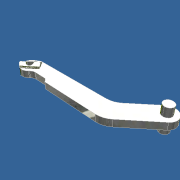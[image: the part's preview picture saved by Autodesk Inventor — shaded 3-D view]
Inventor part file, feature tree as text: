
AUTODESK INVENTOR PART (.ipt)
format: ipt  version: unknown  size: 225,280 bytes
history: native  units: mm
features: extrude x5, sketch x5, other x1
ambient origin geometry x8: Origin, YZ Plane, XZ Plane, XY Plane, X Axis, Y Axis, Z Axis, Center Point
feature tree (11):
  extrude  "Выдавливание1"  Depth=1.2mm
  extrude  "Выдавливание2"  Depth=5.0mm
  other  "РабПлоскость1"
  extrude  "Выдавливание3"  Depth=3.0mm
  extrude  "Выдавливание4"  Depth=2.0mm
  extrude  "Выдавливание5"  Depth=4.0mm
  sketch  "Эскиз1"
  sketch  "Эскиз2"
  sketch  "Эскиз3"
  sketch  "Эскиз4"
  sketch  "Эскиз5"
